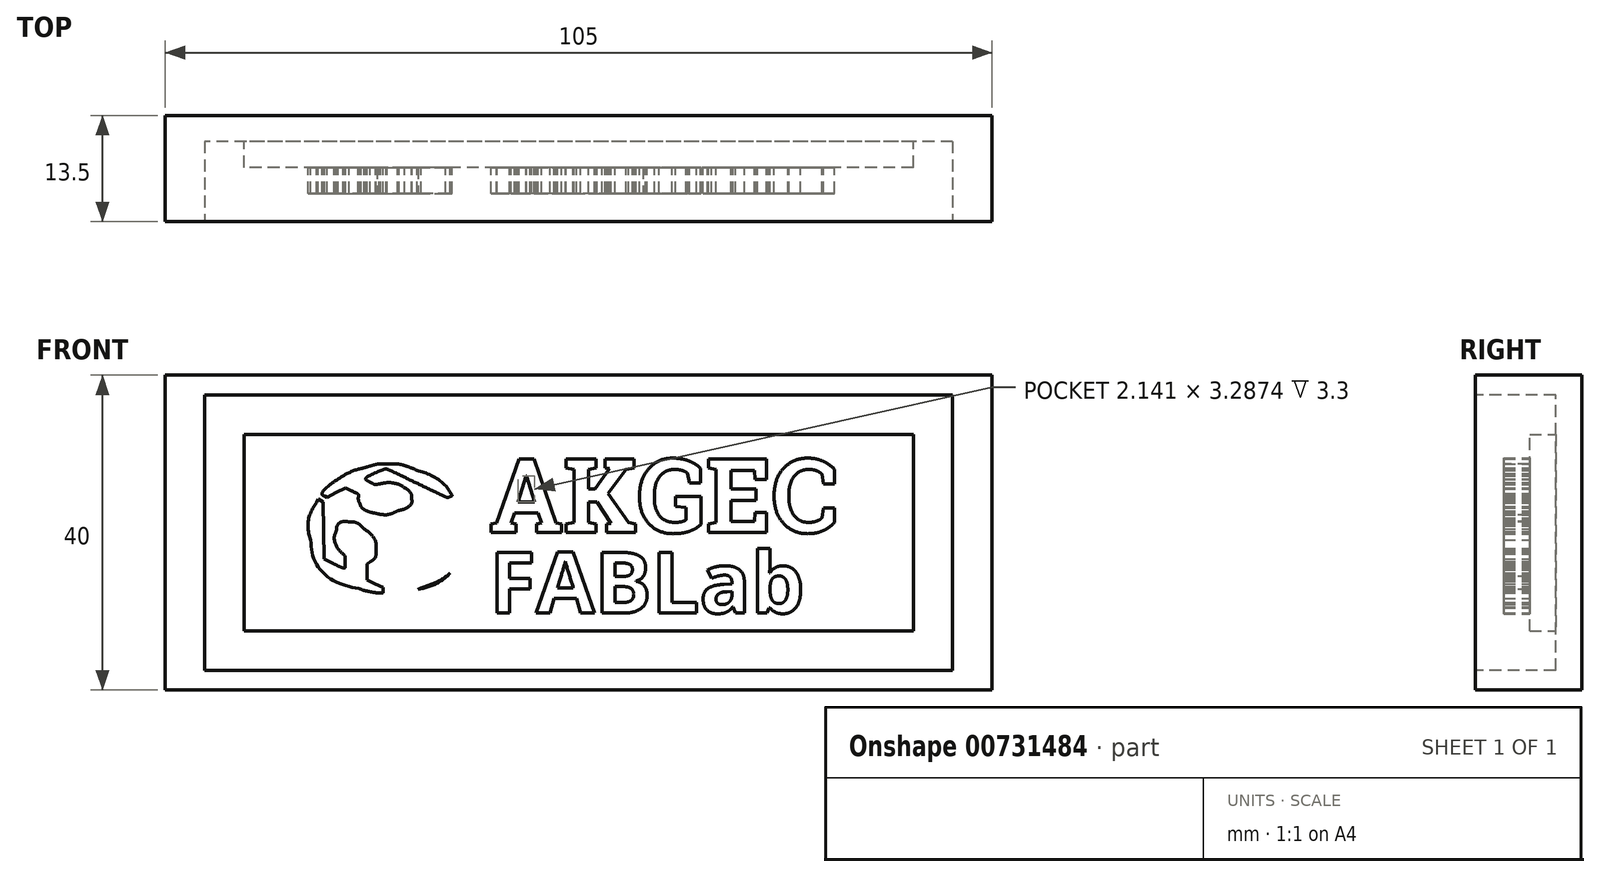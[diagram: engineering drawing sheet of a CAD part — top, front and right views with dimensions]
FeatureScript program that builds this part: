
annotation { "Feature Type Name" : "Feature", "Feature Type Description" : "" }
export const myFeature = defineFeature(function(context is Context, id is Id, definition is map)
    precondition{}
    {
        {
            var Q0;
            Q0=qCreatedBy(makeId("Front.planeOp"),FACE);
            var sketch = newSketch(context, id + "F0", { "sketchPlane" : qUnion([Q0])});
            skLineSegment(sketch, "E0.bottom", {"start": v(55, -20) * mm, "end": v(-50, -20) * mm});
            skLineSegment(sketch, "E0.top", {"start": v(55, 20) * mm, "end": v(-50, 20) * mm});
            skLineSegment(sketch, "E0.left", {"start": v(55, -20) * mm, "end": v(55, 20) * mm});
            skPoint(sketch, "E0.middle", {"position": v(0, 0) * mm});
            skLineSegment(sketch, "E1", {"start": v(-50, 20) * mm, "end": v(-50, -20) * mm});
            skPoint(sketch, "E2.orphan", {"position": v(-55, -20) * mm});
            skPoint(sketch, "E3.orphan", {"position": v(-55, 20) * mm});
            skSolve(sketch);
        }
        {
            var Q0;
            Q0 = qSketchRegion(id + "F0", true);
            extrude(context, id + "F1", {"entities" : qUnion([Q0]), "depth" : 13.5 * mm, "offsetDistance" : 25 * mm});
        }
        {
            var Q0;
            Q0=makeQuery(id+"F1.opExtrude","CAP_FACE",FACE,{"disambiguationData":[OSD([sQuery(id+"F0.wireOp",EDGE,"E0.bottom"),sQuery(id+"F0.wireOp",EDGE,"E0.top"),sQuery(id+"F0.wireOp",EDGE,"E0.left"),sQuery(id+"F0.wireOp",EDGE,"E0.right")])],"isStart":false});
            var sketch = newSketch(context, id + "F2", { "sketchPlane" : qUnion([Q0])});
            skLineSegment(sketch, "E4.bottom", {"start": v(50, -17.5) * mm, "end": v(-45, -17.5) * mm});
            skLineSegment(sketch, "E4.top", {"start": v(50, 17.5) * mm, "end": v(-45, 17.5) * mm});
            skLineSegment(sketch, "E4.left", {"start": v(50, -17.5) * mm, "end": v(50, 17.5) * mm});
            skPoint(sketch, "E4.middle", {"position": v(0, 0) * mm});
            skLineSegment(sketch, "E5", {"start": v(-45, 17.5) * mm, "end": v(-45, -17.5) * mm});
            skPoint(sketch, "E6.orphan", {"position": v(-50, -17.5) * mm});
            skPoint(sketch, "E7.orphan", {"position": v(-50, 17.5) * mm});
            skSolve(sketch);
        }
        {
            var Q0;
            Q0=makeQuery(id+"F2.imprint","IMPRINT",FACE,{"disambiguationData":[TD([[makeQuery(id+"F2.imprint","IMPRINT",EDGE,{"derivedFrom":sQuery(id+"F2.wireOp",EDGE,"E4.bottom")}),-1.0]])]});
            extrude(context, id + "F3", {"entities" : qUnion([Q0]), "operationType" : NewBodyOperationType.REMOVE, "oppositeDirection" : true, "depth" : 10.2 * mm, "offsetDistance" : 25 * mm});
        }
        {
            var Q0;
            Q0=makeQuery(id+"F3.boolean.opBoolean","COPY",FACE,{"derivedFrom":makeQuery(id+"F3.opExtrude","CAP_FACE",FACE,{"disambiguationData":[OSD([sQuery(id+"F2.wireOp",EDGE,"E4.bottom"),sQuery(id+"F2.wireOp",EDGE,"E4.top"),sQuery(id+"F2.wireOp",EDGE,"E4.left"),sQuery(id+"F2.wireOp",EDGE,"E4.right")])],"isStart":false})});
            var sketch = newSketch(context, id + "F4", { "sketchPlane" : qUnion([Q0])});
            skLineSegment(sketch, "E8.bottom", {"start": v(45, -12.5) * mm, "end": v(-40, -12.5) * mm});
            skLineSegment(sketch, "E8.top", {"start": v(45, 12.5) * mm, "end": v(-40, 12.5) * mm});
            skLineSegment(sketch, "E8.left", {"start": v(45, -12.5) * mm, "end": v(45, 12.5) * mm});
            skPoint(sketch, "E8.middle", {"position": v(0, 0) * mm});
            skLineSegment(sketch, "E9", {"start": v(-40, 12.5) * mm, "end": v(-40, -12.5) * mm});
            skPoint(sketch, "E8.right.end.orphan", {"position": v(-45, 12.5) * mm});
            skPoint(sketch, "E10.orphan", {"position": v(-45, -12.5) * mm});
            skSolve(sketch);
        }
        {
            var Q0;
            Q0=makeQuery(id+"F4.imprint","IMPRINT",FACE,{"disambiguationData":[TD([[makeQuery(id+"F4.imprint","IMPRINT",EDGE,{"derivedFrom":sQuery(id+"F4.wireOp",EDGE,"E8.bottom")}),-1.0]])]});
            extrude(context, id + "F5", {"entities" : qUnion([Q0]), "operationType" : NewBodyOperationType.ADD, "depth" : 3.3 * mm, "offsetDistance" : 25 * mm});
        }
        {
            var Q0;
            Q0=makeQuery(id+"F5.opExtrude","CAP_FACE",FACE,{"disambiguationData":[OSD([sQuery(id+"F4.wireOp",EDGE,"E8.bottom"),sQuery(id+"F4.wireOp",EDGE,"E8.top"),sQuery(id+"F4.wireOp",EDGE,"E8.left"),sQuery(id+"F4.wireOp",EDGE,"E8.right")])],"isStart":false});
            var sketch = newSketch(context, id + "F6", { "sketchPlane" : qUnion([Q0])});
            skText(sketch, "E11", { "text": "AKGEC\n", "fontName": "RobotoSlab-Bold.ttf"});
            const initialGuessF6  = {"E11": [-0.00887, 0, 1, 0, 0.00945]};
            skSetInitialGuess(sketch, initialGuessF6);
            skSolve(sketch);
        }
        {
            var Q0;
            Q0=makeQuery(id+"F6.imprint","IMPRINT",FACE,{"disambiguationData":[TD([[makeQuery(id+"F6.imprint","IMPRINT",EDGE,{"derivedFrom":sQuery(id+"F6.wireOp",EDGE,"E11.sketch_text.stroke-0")}),1.0]])]});
            var sketch = newSketch(context, id + "F7", { "sketchPlane" : qUnion([Q0])});
            skText(sketch, "E12", { "text": "FABLab", "fontName": "OpenSans-Bold.ttf"});
            const initialGuessF7  = {"E12": [-0.00883, -0.01021, 1, 0, 0.00776]};
            skSetInitialGuess(sketch, initialGuessF7);
            skSolve(sketch);
        }
        {
            var Q0;
            Q0 = qSketchRegion(id + "F6", true);
            extrude(context, id + "F8", {"entities" : qUnion([Q0]), "operationType" : NewBodyOperationType.ADD, "depth" : 3.3 * mm, "offsetDistance" : 25 * mm});
        }
        {
            var Q0;
            Q0 = qSketchRegion(id + "F7", true);
            extrude(context, id + "F9", {"entities" : qUnion([Q0]), "operationType" : NewBodyOperationType.ADD, "depth" : 3.3 * mm, "offsetDistance" : 25 * mm});
        }
        {
            var Q0;
            {var subQ53=sQuery(id+"F4.wireOp",EDGE,"E8.left");var subQ57=sQuery(id+"F4.wireOp",EDGE,"E8.top");var subQ61=sQuery(id+"F4.wireOp",EDGE,"E8.right");var subQ68=sQuery(id+"F4.wireOp",EDGE,"E8.bottom");var subQ69=makeQuery(id+"F5.opExtrude","SWEPT_FACE",FACE,{"disambiguationData":[OSD([subQ68])]});Q0=makeQuery(id+"F9.boolean.opBoolean","SPLIT",FACE,{"disambiguationData":[TD([subQ69])],"derivedFrom":makeQuery(id+"F8.boolean.opBoolean","SPLIT",FACE,{"disambiguationData":[TD([subQ69])],"derivedFrom":makeQuery(id+"F5.opExtrude","CAP_FACE",FACE,{"disambiguationData":[OSD([subQ68,subQ57,subQ53,subQ61])],"isStart":false})})});}
            var sketch = newSketch(context, id + "F10", { "sketchPlane" : qUnion([Q0])});
            skFitSpline(sketch, "E13", {"points": [v(-25.16, -9.86) * mm, v(-25.16, -8.7) * mm, v(-25.14, -8.5) * mm, v(-25, -8.45) * mm]});
            skFitSpline(sketch, "E14", {"points": [v(-25, -8.45) * mm, v(-24.7, -8.36) * mm, v(-23.55, -8.4) * mm, v(-23.2, -8.52) * mm]});
            skFitSpline(sketch, "E15", {"points": [v(-23.2, -8.52) * mm, v(-22.66, -8.7) * mm, v(-22.49, -9.17) * mm, v(-22.81, -9.55) * mm]});
            skFitSpline(sketch, "E16", {"points": [v(-22.81, -9.55) * mm, v(-22.92, -9.67) * mm, v(-22.94, -9.77) * mm, v(-22.88, -9.8) * mm]});
            skFitSpline(sketch, "E17", {"points": [v(-22.88, -9.8) * mm, v(-22.83, -9.83) * mm, v(-22.73, -9.94) * mm, v(-22.67, -10.04) * mm]});
            skFitSpline(sketch, "E18", {"points": [v(-22.67, -10.04) * mm, v(-22.33, -10.56) * mm, v(-22.77, -11.1) * mm, v(-23.64, -11.23) * mm]});
            skFitSpline(sketch, "E19", {"points": [v(-23.64, -11.23) * mm, v(-23.94, -11.28) * mm, v(-24.26, -11.3) * mm, v(-24.35, -11.3) * mm]});
            skFitSpline(sketch, "E20", {"points": [v(-24.35, -11.3) * mm, v(-24.44, -11.3) * mm, v(-24.66, -11.27) * mm, v(-24.84, -11.25) * mm]});
            skLineSegment(sketch, "E21", {"start": v(-24.84, -11.25) * mm, "end": v(-25.16, -11.22) * mm});
            skLineSegment(sketch, "E22", {"start": v(-25.16, -11.22) * mm, "end": v(-25.16, -9.86) * mm});
            skFitSpline(sketch, "E23", {"points": [v(-23.1, -10.81) * mm, v(-22.95, -10.7) * mm, v(-22.85, -10.52) * mm, v(-22.85, -10.39) * mm]});
            skFitSpline(sketch, "E24", {"points": [v(-22.85, -10.39) * mm, v(-22.85, -10.16) * mm, v(-23.07, -9.9) * mm, v(-23.26, -9.9) * mm]});
            skFitSpline(sketch, "E25", {"points": [v(-23.26, -9.9) * mm, v(-23.44, -9.9) * mm, v(-23.36, -9.6) * mm, v(-23.15, -9.5) * mm]});
            skFitSpline(sketch, "E26", {"points": [v(-23.15, -9.5) * mm, v(-22.89, -9.36) * mm, v(-22.9, -9.03) * mm, v(-23.17, -8.82) * mm]});
            skFitSpline(sketch, "E27", {"points": [v(-23.17, -8.82) * mm, v(-23.35, -8.68) * mm, v(-23.53, -8.65) * mm, v(-24.13, -8.65) * mm]});
            skFitSpline(sketch, "E28", {"points": [v(-24.1, -11.04) * mm, v(-23.5, -11.01) * mm, v(-23.3, -10.97) * mm, v(-23.1, -10.81) * mm]});
            skLineSegment(sketch, "E29", {"start": v(-24.13, -8.65) * mm, "end": v(-24.86, -8.65) * mm});
            skLineSegment(sketch, "E30", {"start": v(-24.86, -8.65) * mm, "end": v(-24.86, -9.87) * mm});
            skLineSegment(sketch, "E31", {"start": v(-24.86, -9.87) * mm, "end": v(-24.86, -11.08) * mm});
            skLineSegment(sketch, "E32", {"start": v(-24.86, -11.08) * mm, "end": v(-24.1, -11.04) * mm});
            skFitSpline(sketch, "E33", {"points": [v(-23.99, -9.91) * mm, v(-23.6, -9.93) * mm, v(-23.49, -9.98) * mm, v(-23.36, -10.16) * mm]});
            skFitSpline(sketch, "E34", {"points": [v(-23.36, -10.16) * mm, v(-23.23, -10.35) * mm, v(-23.23, -10.4) * mm, v(-23.39, -10.6) * mm]});
            skFitSpline(sketch, "E35", {"points": [v(-23.39, -10.6) * mm, v(-23.53, -10.78) * mm, v(-23.64, -10.81) * mm, v(-24.01, -10.81) * mm]});
            skLineSegment(sketch, "E36", {"start": v(-24.46, -10.35) * mm, "end": v(-24.46, -9.89) * mm});
            skLineSegment(sketch, "E37", {"start": v(-24.46, -9.89) * mm, "end": v(-23.99, -9.91) * mm});
            skFitSpline(sketch, "E38", {"points": [v(-23.62, -10.45) * mm, v(-23.53, -10.33) * mm, v(-23.54, -10.28) * mm, v(-23.7, -10.18) * mm]});
            skFitSpline(sketch, "E39", {"points": [v(-23.7, -10.18) * mm, v(-24.02, -9.98) * mm, v(-24.16, -10.04) * mm, v(-24.16, -10.36) * mm]});
            skFitSpline(sketch, "E40", {"points": [v(-24.16, -10.36) * mm, v(-24.16, -10.62) * mm, v(-24.13, -10.65) * mm, v(-23.94, -10.63) * mm]});
            skFitSpline(sketch, "E41", {"points": [v(-23.94, -10.63) * mm, v(-23.82, -10.62) * mm, v(-23.68, -10.54) * mm, v(-23.62, -10.45) * mm]});
            skLineSegment(sketch, "E42", {"start": v(-24.01, -10.81) * mm, "end": v(-24.46, -10.81) * mm});
            skLineSegment(sketch, "E43", {"start": v(-24.46, -10.81) * mm, "end": v(-24.46, -10.35) * mm});
            skFitSpline(sketch, "E44", {"points": [v(-24.07, -8.82) * mm, v(-23.64, -8.82) * mm, v(-23.35, -8.98) * mm, v(-23.35, -9.23) * mm]});
            skFitSpline(sketch, "E45", {"points": [v(-23.35, -9.23) * mm, v(-23.35, -9.48) * mm, v(-23.64, -9.65) * mm, v(-24.07, -9.65) * mm]});
            skLineSegment(sketch, "E46", {"start": v(-24.46, -9.23) * mm, "end": v(-24.46, -8.82) * mm});
            skLineSegment(sketch, "E47", {"start": v(-24.46, -8.82) * mm, "end": v(-24.07, -8.82) * mm});
            skFitSpline(sketch, "E48", {"points": [v(-23.82, -9.43) * mm, v(-23.55, -9.35) * mm, v(-23.62, -9.07) * mm, v(-23.9, -9.07) * mm]});
            skFitSpline(sketch, "E49", {"points": [v(-23.9, -9.07) * mm, v(-24.1, -9.07) * mm, v(-24.16, -9.1) * mm, v(-24.16, -9.27) * mm]});
            skFitSpline(sketch, "E50", {"points": [v(-24.16, -9.27) * mm, v(-24.16, -9.49) * mm, v(-24.1, -9.52) * mm, v(-23.82, -9.43) * mm]});
            skLineSegment(sketch, "E51", {"start": v(-24.07, -9.65) * mm, "end": v(-24.46, -9.65) * mm});
            skLineSegment(sketch, "E52", {"start": v(-24.46, -9.65) * mm, "end": v(-24.46, -9.23) * mm});
            skFitSpline(sketch, "E53", {"points": [v(-15.81, -9.86) * mm, v(-15.81, -8.7) * mm, v(-15.79, -8.5) * mm, v(-15.65, -8.45) * mm]});
            skFitSpline(sketch, "E54", {"points": [v(-15.65, -8.45) * mm, v(-15.36, -8.36) * mm, v(-14.2, -8.4) * mm, v(-13.86, -8.52) * mm]});
            skFitSpline(sketch, "E55", {"points": [v(-13.86, -8.52) * mm, v(-13.3, -8.7) * mm, v(-13.13, -9.17) * mm, v(-13.46, -9.55) * mm]});
            skFitSpline(sketch, "E56", {"points": [v(-13.46, -9.55) * mm, v(-13.56, -9.67) * mm, v(-13.59, -9.77) * mm, v(-13.53, -9.8) * mm]});
            skFitSpline(sketch, "E57", {"points": [v(-13.53, -9.8) * mm, v(-13.47, -9.83) * mm, v(-13.38, -9.94) * mm, v(-13.31, -10.04) * mm]});
            skFitSpline(sketch, "E58", {"points": [v(-13.31, -10.04) * mm, v(-12.98, -10.56) * mm, v(-13.42, -11.1) * mm, v(-14.3, -11.23) * mm]});
            skFitSpline(sketch, "E59", {"points": [v(-14.3, -11.23) * mm, v(-14.6, -11.28) * mm, v(-14.9, -11.3) * mm, v(-15, -11.3) * mm]});
            skFitSpline(sketch, "E60", {"points": [v(-15, -11.3) * mm, v(-15.09, -11.3) * mm, v(-15.3, -11.27) * mm, v(-15.49, -11.25) * mm]});
            skLineSegment(sketch, "E61", {"start": v(-15.49, -11.25) * mm, "end": v(-15.81, -11.22) * mm});
            skLineSegment(sketch, "E62", {"start": v(-15.81, -11.22) * mm, "end": v(-15.81, -9.86) * mm});
            skFitSpline(sketch, "E63", {"points": [v(-13.75, -10.81) * mm, v(-13.6, -10.7) * mm, v(-13.5, -10.52) * mm, v(-13.5, -10.39) * mm]});
            skFitSpline(sketch, "E64", {"points": [v(-13.5, -10.39) * mm, v(-13.5, -10.16) * mm, v(-13.72, -9.9) * mm, v(-13.9, -9.9) * mm]});
            skFitSpline(sketch, "E65", {"points": [v(-13.9, -9.9) * mm, v(-14.08, -9.9) * mm, v(-14, -9.6) * mm, v(-13.8, -9.5) * mm]});
            skFitSpline(sketch, "E66", {"points": [v(-13.8, -9.5) * mm, v(-13.54, -9.36) * mm, v(-13.55, -9.03) * mm, v(-13.82, -8.82) * mm]});
            skFitSpline(sketch, "E67", {"points": [v(-13.82, -8.82) * mm, v(-14, -8.68) * mm, v(-14.18, -8.65) * mm, v(-14.78, -8.65) * mm]});
            skFitSpline(sketch, "E68", {"points": [v(-14.75, -11.04) * mm, v(-14.14, -11.01) * mm, v(-13.95, -10.97) * mm, v(-13.75, -10.81) * mm]});
            skLineSegment(sketch, "E69", {"start": v(-14.78, -8.65) * mm, "end": v(-15.51, -8.65) * mm});
            skLineSegment(sketch, "E70", {"start": v(-15.51, -8.65) * mm, "end": v(-15.51, -9.87) * mm});
            skLineSegment(sketch, "E71", {"start": v(-15.51, -9.87) * mm, "end": v(-15.51, -11.08) * mm});
            skLineSegment(sketch, "E72", {"start": v(-15.51, -11.08) * mm, "end": v(-14.75, -11.04) * mm});
            skFitSpline(sketch, "E73", {"points": [v(-14.63, -9.91) * mm, v(-14.24, -9.93) * mm, v(-14.13, -9.98) * mm, v(-14.01, -10.16) * mm]});
            skFitSpline(sketch, "E74", {"points": [v(-14.01, -10.16) * mm, v(-13.88, -10.35) * mm, v(-13.88, -10.4) * mm, v(-14.04, -10.6) * mm]});
            skFitSpline(sketch, "E75", {"points": [v(-14.04, -10.6) * mm, v(-14.18, -10.78) * mm, v(-14.28, -10.81) * mm, v(-14.66, -10.81) * mm]});
            skLineSegment(sketch, "E76", {"start": v(-15.1, -10.35) * mm, "end": v(-15.1, -9.89) * mm});
            skLineSegment(sketch, "E77", {"start": v(-15.1, -9.89) * mm, "end": v(-14.63, -9.91) * mm});
            skFitSpline(sketch, "E78", {"points": [v(-14.26, -10.45) * mm, v(-14.18, -10.33) * mm, v(-14.2, -10.28) * mm, v(-14.35, -10.18) * mm]});
            skFitSpline(sketch, "E79", {"points": [v(-14.35, -10.18) * mm, v(-14.67, -9.98) * mm, v(-14.8, -10.04) * mm, v(-14.8, -10.36) * mm]});
            skFitSpline(sketch, "E80", {"points": [v(-14.8, -10.36) * mm, v(-14.8, -10.62) * mm, v(-14.78, -10.65) * mm, v(-14.6, -10.63) * mm]});
            skFitSpline(sketch, "E81", {"points": [v(-14.6, -10.63) * mm, v(-14.47, -10.62) * mm, v(-14.33, -10.54) * mm, v(-14.26, -10.45) * mm]});
            skLineSegment(sketch, "E82", {"start": v(-14.66, -10.81) * mm, "end": v(-15.1, -10.81) * mm});
            skLineSegment(sketch, "E83", {"start": v(-15.1, -10.81) * mm, "end": v(-15.1, -10.35) * mm});
            skFitSpline(sketch, "E84", {"points": [v(-14.71, -8.82) * mm, v(-14.29, -8.82) * mm, v(-14, -8.98) * mm, v(-14, -9.23) * mm]});
            skFitSpline(sketch, "E85", {"points": [v(-14, -9.23) * mm, v(-14, -9.48) * mm, v(-14.29, -9.65) * mm, v(-14.71, -9.65) * mm]});
            skLineSegment(sketch, "E86", {"start": v(-15.1, -9.23) * mm, "end": v(-15.1, -8.82) * mm});
            skLineSegment(sketch, "E87", {"start": v(-15.1, -8.82) * mm, "end": v(-14.71, -8.82) * mm});
            skFitSpline(sketch, "E88", {"points": [v(-14.46, -9.43) * mm, v(-14.2, -9.35) * mm, v(-14.27, -9.07) * mm, v(-14.56, -9.07) * mm]});
            skFitSpline(sketch, "E89", {"points": [v(-14.56, -9.07) * mm, v(-14.76, -9.07) * mm, v(-14.8, -9.1) * mm, v(-14.8, -9.27) * mm]});
            skFitSpline(sketch, "E90", {"points": [v(-14.8, -9.27) * mm, v(-14.8, -9.49) * mm, v(-14.74, -9.52) * mm, v(-14.46, -9.43) * mm]});
            skLineSegment(sketch, "E91", {"start": v(-14.71, -9.65) * mm, "end": v(-15.1, -9.65) * mm});
            skLineSegment(sketch, "E92", {"start": v(-15.1, -9.65) * mm, "end": v(-15.1, -9.23) * mm});
            skFitSpline(sketch, "E93", {"points": [v(-28.89, -9.07) * mm, v(-29.46, -9.07) * mm, v(-29.49, -9.07) * mm, v(-29.49, -9.27) * mm]});
            skFitSpline(sketch, "E94", {"points": [v(-29.49, -9.27) * mm, v(-29.49, -9.47) * mm, v(-29.46, -9.48) * mm, v(-28.94, -9.48) * mm]});
            skFitSpline(sketch, "E95", {"points": [v(-28.94, -9.48) * mm, v(-28.43, -9.48) * mm, v(-28.38, -9.5) * mm, v(-28.32, -9.69) * mm]});
            skFitSpline(sketch, "E96", {"points": [v(-28.32, -9.69) * mm, v(-28.21, -10.06) * mm, v(-28.33, -10.15) * mm, v(-28.93, -10.15) * mm]});
            skLineSegment(sketch, "E97", {"start": v(-30.4, -9.81) * mm, "end": v(-30.4, -8.4) * mm});
            skLineSegment(sketch, "E98", {"start": v(-30.4, -8.4) * mm, "end": v(-29.34, -8.4) * mm});
            skLineSegment(sketch, "E99", {"start": v(-29.34, -8.4) * mm, "end": v(-28.28, -8.4) * mm});
            skLineSegment(sketch, "E100", {"start": v(-28.28, -8.4) * mm, "end": v(-28.28, -8.73) * mm});
            skLineSegment(sketch, "E101", {"start": v(-28.28, -8.73) * mm, "end": v(-28.28, -9.07) * mm});
            skLineSegment(sketch, "E102", {"start": v(-28.28, -9.07) * mm, "end": v(-28.89, -9.07) * mm});
            skLineSegment(sketch, "E103", {"start": v(-28.93, -10.15) * mm, "end": v(-29.49, -10.15) * mm});
            skLineSegment(sketch, "E104", {"start": v(-29.49, -10.15) * mm, "end": v(-29.49, -10.69) * mm});
            skLineSegment(sketch, "E105", {"start": v(-29.49, -10.69) * mm, "end": v(-29.49, -11.23) * mm});
            skLineSegment(sketch, "E106", {"start": v(-29.49, -11.23) * mm, "end": v(-29.94, -11.23) * mm});
            skLineSegment(sketch, "E107", {"start": v(-29.94, -11.23) * mm, "end": v(-30.4, -11.23) * mm});
            skLineSegment(sketch, "E108", {"start": v(-30.4, -11.23) * mm, "end": v(-30.4, -9.81) * mm});
            skFitSpline(sketch, "E109", {"points": [v(-29.14, -9.98) * mm, v(-28.71, -9.98) * mm, v(-28.58, -9.95) * mm, v(-28.58, -9.86) * mm]});
            skFitSpline(sketch, "E110", {"points": [v(-28.58, -9.86) * mm, v(-28.58, -9.76) * mm, v(-28.71, -9.73) * mm, v(-29.14, -9.73) * mm]});
            skLineSegment(sketch, "E111", {"start": v(-29.69, -10.52) * mm, "end": v(-29.69, -9.98) * mm});
            skLineSegment(sketch, "E112", {"start": v(-29.69, -9.98) * mm, "end": v(-29.14, -9.98) * mm});
            skFitSpline(sketch, "E113", {"points": [v(-29.09, -8.9) * mm, v(-28.62, -8.9) * mm, v(-28.48, -8.87) * mm, v(-28.48, -8.77) * mm]});
            skFitSpline(sketch, "E114", {"points": [v(-28.48, -8.77) * mm, v(-28.48, -8.67) * mm, v(-28.64, -8.65) * mm, v(-29.34, -8.65) * mm]});
            skLineSegment(sketch, "E115", {"start": v(-29.14, -9.73) * mm, "end": v(-29.69, -9.73) * mm});
            skLineSegment(sketch, "E116", {"start": v(-29.69, -9.73) * mm, "end": v(-29.69, -9.31) * mm});
            skLineSegment(sketch, "E117", {"start": v(-29.69, -9.31) * mm, "end": v(-29.69, -8.9) * mm});
            skLineSegment(sketch, "E118", {"start": v(-29.69, -8.9) * mm, "end": v(-29.09, -8.9) * mm});
            skFitSpline(sketch, "E119", {"points": [v(-29.94, -11.06) * mm, v(-29.7, -11.06) * mm, v(-29.69, -11.04) * mm, v(-29.69, -10.52) * mm]});
            skLineSegment(sketch, "E120", {"start": v(-29.34, -8.65) * mm, "end": v(-30.2, -8.65) * mm});
            skLineSegment(sketch, "E121", {"start": v(-30.2, -8.65) * mm, "end": v(-30.2, -9.86) * mm});
            skLineSegment(sketch, "E122", {"start": v(-30.2, -9.86) * mm, "end": v(-30.2, -11.06) * mm});
            skLineSegment(sketch, "E123", {"start": v(-30.2, -11.06) * mm, "end": v(-29.94, -11.06) * mm});
            skFitSpline(sketch, "E124", {"points": [v(-28.48, -11.16) * mm, v(-28.48, -11.12) * mm, v(-28.42, -10.93) * mm, v(-28.34, -10.72) * mm]});
            skFitSpline(sketch, "E125", {"points": [v(-28.34, -10.72) * mm, v(-28.26, -10.52) * mm, v(-28.03, -9.91) * mm, v(-27.83, -9.37) * mm]});
            skFitSpline(sketch, "E126", {"points": [v(-25.86, -9.73) * mm, v(-25.59, -10.44) * mm, v(-25.37, -11.07) * mm, v(-25.37, -11.13) * mm]});
            skFitSpline(sketch, "E127", {"points": [v(-25.37, -11.13) * mm, v(-25.37, -11.2) * mm, v(-25.53, -11.23) * mm, v(-25.85, -11.23) * mm]});
            skFitSpline(sketch, "E128", {"points": [v(-25.85, -11.23) * mm, v(-26.33, -11.23) * mm, v(-26.34, -11.23) * mm, v(-26.46, -10.9) * mm]});
            skFitSpline(sketch, "E129", {"points": [v(-26.46, -10.9) * mm, v(-26.58, -10.57) * mm, v(-26.6, -10.55) * mm, v(-26.95, -10.58) * mm]});
            skFitSpline(sketch, "E130", {"points": [v(-26.95, -10.58) * mm, v(-27.29, -10.6) * mm, v(-27.33, -10.63) * mm, v(-27.4, -10.92) * mm]});
            skFitSpline(sketch, "E131", {"points": [v(-27.4, -10.92) * mm, v(-27.5, -11.23) * mm, v(-27.5, -11.23) * mm, v(-28, -11.23) * mm]});
            skFitSpline(sketch, "E132", {"points": [v(-28, -11.23) * mm, v(-28.26, -11.23) * mm, v(-28.48, -11.2) * mm, v(-28.48, -11.16) * mm]});
            skLineSegment(sketch, "E133", {"start": v(-27.83, -9.37) * mm, "end": v(-27.47, -8.4) * mm});
            skLineSegment(sketch, "E134", {"start": v(-27.47, -8.4) * mm, "end": v(-26.9, -8.42) * mm});
            skLineSegment(sketch, "E135", {"start": v(-26.9, -8.42) * mm, "end": v(-26.34, -8.44) * mm});
            skLineSegment(sketch, "E136", {"start": v(-26.34, -8.44) * mm, "end": v(-25.86, -9.73) * mm});
            skFitSpline(sketch, "E137", {"points": [v(-26.23, -10.75) * mm, v(-26.15, -11) * mm, v(-26.09, -11.06) * mm, v(-25.9, -11.06) * mm]});
            skFitSpline(sketch, "E138", {"points": [v(-25.9, -11.06) * mm, v(-25.77, -11.06) * mm, v(-25.67, -11.05) * mm, v(-25.67, -11.04) * mm]});
            skFitSpline(sketch, "E139", {"points": [v(-25.67, -11.04) * mm, v(-25.67, -11.03) * mm, v(-25.86, -10.5) * mm, v(-26.1, -9.86) * mm]});
            skLineSegment(sketch, "E140", {"start": v(-27.63, -10.73) * mm, "end": v(-27.56, -10.39) * mm});
            skLineSegment(sketch, "E141", {"start": v(-27.56, -10.39) * mm, "end": v(-26.94, -10.41) * mm});
            skLineSegment(sketch, "E142", {"start": v(-26.94, -10.41) * mm, "end": v(-26.32, -10.44) * mm});
            skLineSegment(sketch, "E143", {"start": v(-26.32, -10.44) * mm, "end": v(-26.23, -10.75) * mm});
            skFitSpline(sketch, "E144", {"points": [v(-27.6, -9.48) * mm, v(-27.75, -9.92) * mm, v(-27.95, -10.45) * mm, v(-28.03, -10.67) * mm]});
            skFitSpline(sketch, "E145", {"points": [v(-28.03, -10.67) * mm, v(-28.17, -11.06) * mm, v(-28.17, -11.06) * mm, v(-27.93, -11.06) * mm]});
            skFitSpline(sketch, "E146", {"points": [v(-27.93, -11.06) * mm, v(-27.73, -11.06) * mm, v(-27.68, -11) * mm, v(-27.63, -10.73) * mm]});
            skLineSegment(sketch, "E147", {"start": v(-26.1, -9.86) * mm, "end": v(-26.53, -8.7) * mm});
            skLineSegment(sketch, "E148", {"start": v(-26.53, -8.7) * mm, "end": v(-26.92, -8.7) * mm});
            skLineSegment(sketch, "E149", {"start": v(-26.92, -8.7) * mm, "end": v(-27.3, -8.7) * mm});
            skLineSegment(sketch, "E150", {"start": v(-27.3, -8.7) * mm, "end": v(-27.6, -9.48) * mm});
            skFitSpline(sketch, "E151", {"points": [v(-27.34, -9.83) * mm, v(-27.23, -9.27) * mm, v(-27.07, -8.9) * mm, v(-26.94, -8.9) * mm]});
            skFitSpline(sketch, "E152", {"points": [v(-26.94, -8.9) * mm, v(-26.86, -8.9) * mm, v(-26.73, -9.12) * mm, v(-26.64, -9.4) * mm]});
            skFitSpline(sketch, "E153", {"points": [v(-26.64, -9.4) * mm, v(-26.4, -10.13) * mm, v(-26.4, -10.15) * mm, v(-26.94, -10.15) * mm]});
            skLineSegment(sketch, "E154", {"start": v(-5.73, -9.43) * mm, "end": v(-5.73, -9.43) * mm});
            skFitSpline(sketch, "E155", {"points": [v(-26.81, -9.77) * mm, v(-26.85, -9.7) * mm, v(-26.88, -9.57) * mm, v(-26.88, -9.5) * mm]});
            skFitSpline(sketch, "E156", {"points": [v(-26.88, -9.5) * mm, v(-26.89, -9.38) * mm, v(-26.9, -9.39) * mm, v(-26.97, -9.52) * mm]});
            skFitSpline(sketch, "E157", {"points": [v(-26.97, -9.52) * mm, v(-27.1, -9.78) * mm, v(-27.09, -9.9) * mm, v(-26.91, -9.9) * mm]});
            skFitSpline(sketch, "E158", {"points": [v(-26.91, -9.9) * mm, v(-26.8, -9.9) * mm, v(-26.77, -9.85) * mm, v(-26.81, -9.77) * mm]});
            skLineSegment(sketch, "E159", {"start": v(-26.94, -10.15) * mm, "end": v(-27.4, -10.15) * mm});
            skLineSegment(sketch, "E160", {"start": v(-27.4, -10.15) * mm, "end": v(-27.34, -9.83) * mm});
            skLineSegment(sketch, "E161", {"start": v(-4.91, -8.47) * mm, "end": v(-4.91, -8.47) * mm});
            skFitSpline(sketch, "E162", {"points": [v(-20.9, -8.41) * mm, v(-20.66, -8.4) * mm, v(-20.48, -8.43) * mm, v(-20.43, -8.5) * mm]});
            skFitSpline(sketch, "E163", {"points": [v(-20.43, -8.5) * mm, v(-20.38, -8.56) * mm, v(-20.34, -9.05) * mm, v(-20.34, -9.59) * mm]});
            skLineSegment(sketch, "E164", {"start": v(-21.32, -9.83) * mm, "end": v(-21.3, -8.44) * mm});
            skLineSegment(sketch, "E165", {"start": v(-21.3, -8.44) * mm, "end": v(-20.9, -8.41) * mm});
            skFitSpline(sketch, "E166", {"points": [v(-19.73, -10.56) * mm, v(-19.15, -10.56) * mm, v(-19.13, -10.57) * mm, v(-19.12, -10.8) * mm]});
            skFitSpline(sketch, "E167", {"points": [v(-19.12, -10.8) * mm, v(-19.12, -11) * mm, v(-19.1, -10.99) * mm, v(-18.98, -10.69) * mm]});
            skFitSpline(sketch, "E168", {"points": [v(-18.98, -10.69) * mm, v(-18.9, -10.5) * mm, v(-18.68, -9.91) * mm, v(-18.48, -9.37) * mm]});
            skLineSegment(sketch, "E169", {"start": v(-20.34, -9.59) * mm, "end": v(-20.34, -10.56) * mm});
            skLineSegment(sketch, "E170", {"start": v(-20.34, -10.56) * mm, "end": v(-19.73, -10.56) * mm});
            skFitSpline(sketch, "E171", {"points": [v(-16.5, -9.73) * mm, v(-16.24, -10.44) * mm, v(-16.02, -11.07) * mm, v(-16.02, -11.13) * mm]});
            skFitSpline(sketch, "E172", {"points": [v(-16.02, -11.13) * mm, v(-16.01, -11.2) * mm, v(-16.18, -11.23) * mm, v(-16.5, -11.23) * mm]});
            skFitSpline(sketch, "E173", {"points": [v(-16.5, -11.23) * mm, v(-16.98, -11.23) * mm, v(-16.99, -11.23) * mm, v(-17.1, -10.9) * mm]});
            skFitSpline(sketch, "E174", {"points": [v(-17.1, -10.9) * mm, v(-17.23, -10.57) * mm, v(-17.25, -10.55) * mm, v(-17.6, -10.58) * mm]});
            skFitSpline(sketch, "E175", {"points": [v(-17.6, -10.58) * mm, v(-17.93, -10.6) * mm, v(-17.98, -10.63) * mm, v(-18.06, -10.92) * mm]});
            skLineSegment(sketch, "E176", {"start": v(-18.48, -9.37) * mm, "end": v(-18.11, -8.4) * mm});
            skLineSegment(sketch, "E177", {"start": v(-18.11, -8.4) * mm, "end": v(-17.55, -8.42) * mm});
            skLineSegment(sketch, "E178", {"start": v(-17.55, -8.42) * mm, "end": v(-16.99, -8.44) * mm});
            skLineSegment(sketch, "E179", {"start": v(-16.99, -8.44) * mm, "end": v(-16.5, -9.73) * mm});
            skFitSpline(sketch, "E180", {"points": [v(-19.33, -10.9) * mm, v(-19.33, -10.75) * mm, v(-19.4, -10.73) * mm, v(-19.99, -10.73) * mm]});
            skLineSegment(sketch, "E181", {"start": v(-18.06, -10.92) * mm, "end": v(-18.15, -11.23) * mm});
            skLineSegment(sketch, "E182", {"start": v(-18.15, -11.23) * mm, "end": v(-19.75, -11.23) * mm});
            skLineSegment(sketch, "E183", {"start": v(-19.75, -11.23) * mm, "end": v(-21.35, -11.23) * mm});
            skLineSegment(sketch, "E184", {"start": v(-21.35, -11.23) * mm, "end": v(-21.32, -9.83) * mm});
            skLineSegment(sketch, "E185", {"start": v(0.58, -8.53) * mm, "end": v(0.58, -8.53) * mm});
            skFitSpline(sketch, "E186", {"points": [v(-20.64, -9.69) * mm, v(-20.64, -8.7) * mm, v(-20.65, -8.65) * mm, v(-20.84, -8.65) * mm]});
            skFitSpline(sketch, "E187", {"points": [v(-20.84, -8.65) * mm, v(-21.03, -8.65) * mm, v(-21.04, -8.7) * mm, v(-21.04, -9.86) * mm]});
            skLineSegment(sketch, "E188", {"start": v(-19.99, -10.73) * mm, "end": v(-20.64, -10.73) * mm});
            skLineSegment(sketch, "E189", {"start": v(-20.64, -10.73) * mm, "end": v(-20.64, -9.69) * mm});
            skFitSpline(sketch, "E190", {"points": [v(-20.19, -11.06) * mm, v(-19.4, -11.06) * mm, v(-19.33, -11.05) * mm, v(-19.33, -10.9) * mm]});
            skLineSegment(sketch, "E191", {"start": v(-21.04, -9.86) * mm, "end": v(-21.04, -11.06) * mm});
            skLineSegment(sketch, "E192", {"start": v(-21.04, -11.06) * mm, "end": v(-20.19, -11.06) * mm});
            skFitSpline(sketch, "E193", {"points": [v(-16.88, -10.75) * mm, v(-16.8, -11) * mm, v(-16.74, -11.06) * mm, v(-16.55, -11.06) * mm]});
            skFitSpline(sketch, "E194", {"points": [v(-16.55, -11.06) * mm, v(-16.42, -11.06) * mm, v(-16.32, -11.05) * mm, v(-16.32, -11.04) * mm]});
            skFitSpline(sketch, "E195", {"points": [v(-16.32, -11.04) * mm, v(-16.32, -11.03) * mm, v(-16.51, -10.5) * mm, v(-16.75, -9.86) * mm]});
            skLineSegment(sketch, "E196", {"start": v(-18.28, -10.73) * mm, "end": v(-18.2, -10.39) * mm});
            skLineSegment(sketch, "E197", {"start": v(-18.2, -10.39) * mm, "end": v(-17.59, -10.41) * mm});
            skLineSegment(sketch, "E198", {"start": v(-17.59, -10.41) * mm, "end": v(-16.97, -10.44) * mm});
            skLineSegment(sketch, "E199", {"start": v(-16.97, -10.44) * mm, "end": v(-16.88, -10.75) * mm});
            skFitSpline(sketch, "E200", {"points": [v(-18.24, -9.48) * mm, v(-18.4, -9.92) * mm, v(-18.6, -10.45) * mm, v(-18.67, -10.67) * mm]});
            skFitSpline(sketch, "E201", {"points": [v(-18.67, -10.67) * mm, v(-18.82, -11.06) * mm, v(-18.82, -11.06) * mm, v(-18.58, -11.06) * mm]});
            skFitSpline(sketch, "E202", {"points": [v(-18.58, -11.06) * mm, v(-18.38, -11.06) * mm, v(-18.33, -11) * mm, v(-18.28, -10.73) * mm]});
            skLineSegment(sketch, "E203", {"start": v(-16.75, -9.86) * mm, "end": v(-17.18, -8.7) * mm});
            skLineSegment(sketch, "E204", {"start": v(-17.18, -8.7) * mm, "end": v(-17.57, -8.7) * mm});
            skLineSegment(sketch, "E205", {"start": v(-17.57, -8.7) * mm, "end": v(-17.95, -8.7) * mm});
            skLineSegment(sketch, "E206", {"start": v(-17.95, -8.7) * mm, "end": v(-18.24, -9.48) * mm});
            skFitSpline(sketch, "E207", {"points": [v(-17.99, -9.83) * mm, v(-17.88, -9.27) * mm, v(-17.72, -8.9) * mm, v(-17.58, -8.9) * mm]});
            skFitSpline(sketch, "E208", {"points": [v(-17.58, -8.9) * mm, v(-17.51, -8.9) * mm, v(-17.38, -9.12) * mm, v(-17.29, -9.4) * mm]});
            skFitSpline(sketch, "E209", {"points": [v(-17.29, -9.4) * mm, v(-17.04, -10.13) * mm, v(-17.05, -10.15) * mm, v(-17.59, -10.15) * mm]});
            skLineSegment(sketch, "E210", {"start": v(3.62, -9.43) * mm, "end": v(3.62, -9.43) * mm});
            skFitSpline(sketch, "E211", {"points": [v(-17.46, -9.77) * mm, v(-17.5, -9.7) * mm, v(-17.53, -9.57) * mm, v(-17.53, -9.5) * mm]});
            skFitSpline(sketch, "E212", {"points": [v(-17.53, -9.5) * mm, v(-17.54, -9.38) * mm, v(-17.55, -9.39) * mm, v(-17.62, -9.52) * mm]});
            skFitSpline(sketch, "E213", {"points": [v(-17.62, -9.52) * mm, v(-17.76, -9.78) * mm, v(-17.74, -9.9) * mm, v(-17.56, -9.9) * mm]});
            skFitSpline(sketch, "E214", {"points": [v(-17.56, -9.9) * mm, v(-17.46, -9.9) * mm, v(-17.42, -9.85) * mm, v(-17.46, -9.77) * mm]});
            skLineSegment(sketch, "E215", {"start": v(-17.59, -10.15) * mm, "end": v(-18.05, -10.15) * mm});
            skLineSegment(sketch, "E216", {"start": v(-18.05, -10.15) * mm, "end": v(-17.99, -9.83) * mm});
            skFitSpline(sketch, "E217", {"points": [v(-23.95, -7.69) * mm, v(-27.63, -7.03) * mm, v(-30.47, -4.85) * mm, v(-31.56, -1.85) * mm]});
            skFitSpline(sketch, "E218", {"points": [v(-31.56, -1.85) * mm, v(-31.94, -0.8) * mm, v(-32.01, 1.11) * mm, v(-31.72, 2.23) * mm]});
            skFitSpline(sketch, "E219", {"points": [v(-31.72, 2.23) * mm, v(-31.52, 2.97) * mm, v(-31.02, 4.07) * mm, v(-30.76, 4.38) * mm]});
            skFitSpline(sketch, "E220", {"points": [v(-30.76, 4.38) * mm, v(-30.63, 4.52) * mm, v(-30.6, 4.52) * mm, v(-30.16, 4.29) * mm]});
            skLineSegment(sketch, "E221", {"start": v(4.44, -8.47) * mm, "end": v(4.44, -8.47) * mm});
            skFitSpline(sketch, "E222", {"points": [v(-27.5, -3.6) * mm, v(-27.47, -3.05) * mm, v(-27.5, -2.96) * mm, v(-27.72, -2.71) * mm]});
            skFitSpline(sketch, "E223", {"points": [v(-27.72, -2.71) * mm, v(-28.25, -2.14) * mm, v(-28.51, -1.5) * mm, v(-28.56, -0.68) * mm]});
            skFitSpline(sketch, "E224", {"points": [v(-28.56, -0.68) * mm, v(-28.6, 0.03) * mm, v(-28.59, 0.13) * mm, v(-28.34, 0.54) * mm]});
            skFitSpline(sketch, "E225", {"points": [v(-28.34, 0.54) * mm, v(-27.97, 1.17) * mm, v(-27.54, 1.38) * mm, v(-26.67, 1.38) * mm]});
            skFitSpline(sketch, "E226", {"points": [v(-26.67, 1.38) * mm, v(-26.16, 1.37) * mm, v(-25.9, 1.32) * mm, v(-25.47, 1.14) * mm]});
            skFitSpline(sketch, "E227", {"points": [v(-25.47, 1.14) * mm, v(-23.88, 0.46) * mm, v(-22.74, -1.38) * mm, v(-23.05, -2.75) * mm]});
            skFitSpline(sketch, "E228", {"points": [v(-23.05, -2.75) * mm, v(-23.17, -3.26) * mm, v(-23.56, -3.79) * mm, v(-23.91, -3.92) * mm]});
            skFitSpline(sketch, "E229", {"points": [v(-23.91, -3.92) * mm, v(-24.15, -4.01) * mm, v(-24.16, -4.04) * mm, v(-24.16, -4.95) * mm]});
            skLineSegment(sketch, "E230", {"start": v(-30.16, 4.29) * mm, "end": v(-29.69, 4.04) * mm});
            skLineSegment(sketch, "E231", {"start": v(-29.69, 4.04) * mm, "end": v(-29.69, 0.42) * mm});
            skLineSegment(sketch, "E232", {"start": v(-29.69, 0.42) * mm, "end": v(-29.69, -3.2) * mm});
            skLineSegment(sketch, "E233", {"start": v(-29.69, -3.2) * mm, "end": v(-28.6, -3.72) * mm});
            skLineSegment(sketch, "E234", {"start": v(-28.6, -3.72) * mm, "end": v(-27.53, -4.23) * mm});
            skLineSegment(sketch, "E235", {"start": v(-27.53, -4.23) * mm, "end": v(-27.5, -3.6) * mm});
            skFitSpline(sketch, "E236", {"points": [v(-22.73, -7.8) * mm, v(-23.04, -7.8) * mm, v(-23.6, -7.75) * mm, v(-23.95, -7.69) * mm]});
            skLineSegment(sketch, "E237", {"start": v(-24.16, -4.95) * mm, "end": v(-24.16, -5.88) * mm});
            skLineSegment(sketch, "E238", {"start": v(-24.16, -5.88) * mm, "end": v(-23.15, -6.36) * mm});
            skLineSegment(sketch, "E239", {"start": v(-23.15, -6.36) * mm, "end": v(-22.15, -6.84) * mm});
            skLineSegment(sketch, "E240", {"start": v(-22.15, -6.84) * mm, "end": v(-22.15, -7.33) * mm});
            skLineSegment(sketch, "E241", {"start": v(-22.15, -7.33) * mm, "end": v(-22.15, -7.82) * mm});
            skLineSegment(sketch, "E242", {"start": v(-22.15, -7.82) * mm, "end": v(-22.73, -7.8) * mm});
            skLineSegment(sketch, "E243", {"start": v(-2.05, -6.39) * mm, "end": v(-2.05, -6.39) * mm});
            skFitSpline(sketch, "E244", {"points": [v(-24, -3.7) * mm, v(-23.5, -3.38) * mm, v(-23.26, -2.9) * mm, v(-23.26, -2.26) * mm]});
            skFitSpline(sketch, "E245", {"points": [v(-23.26, -2.26) * mm, v(-23.25, -1.29) * mm, v(-23.81, -0.28) * mm, v(-24.77, 0.46) * mm]});
            skFitSpline(sketch, "E246", {"points": [v(-24.77, 0.46) * mm, v(-26.18, 1.55) * mm, v(-27.88, 1.4) * mm, v(-28.3, 0.14) * mm]});
            skFitSpline(sketch, "E247", {"points": [v(-28.3, 0.14) * mm, v(-28.55, -0.64) * mm, v(-28.16, -1.91) * mm, v(-27.42, -2.71) * mm]});
            skFitSpline(sketch, "E248", {"points": [v(-27.42, -2.71) * mm, v(-27.2, -2.95) * mm, v(-27.18, -3.06) * mm, v(-27.18, -3.73) * mm]});
            skFitSpline(sketch, "E249", {"points": [v(-27.18, -3.73) * mm, v(-27.18, -4.4) * mm, v(-27.2, -4.49) * mm, v(-27.35, -4.48) * mm]});
            skFitSpline(sketch, "E250", {"points": [v(-27.35, -4.48) * mm, v(-27.45, -4.48) * mm, v(-28.05, -4.23) * mm, v(-28.68, -3.92) * mm]});
            skLineSegment(sketch, "E251", {"start": v(-22.35, -7.32) * mm, "end": v(-22.35, -6.99) * mm});
            skLineSegment(sketch, "E252", {"start": v(-22.35, -6.99) * mm, "end": v(-23.35, -6.5) * mm});
            skLineSegment(sketch, "E253", {"start": v(-23.35, -6.5) * mm, "end": v(-24.36, -6.03) * mm});
            skLineSegment(sketch, "E254", {"start": v(-24.36, -6.03) * mm, "end": v(-24.36, -4.99) * mm});
            skLineSegment(sketch, "E255", {"start": v(-24.36, -4.99) * mm, "end": v(-24.36, -3.95) * mm});
            skLineSegment(sketch, "E256", {"start": v(-24.36, -3.95) * mm, "end": v(-24, -3.7) * mm});
            skFitSpline(sketch, "E257", {"points": [v(-30.8, 3.86) * mm, v(-31.65, 2.27) * mm, v(-31.9, 0.69) * mm, v(-31.55, -0.94) * mm]});
            skFitSpline(sketch, "E258", {"points": [v(-31.55, -0.94) * mm, v(-30.96, -3.76) * mm, v(-28.62, -6.1) * mm, v(-25.41, -7.12) * mm]});
            skFitSpline(sketch, "E259", {"points": [v(-25.41, -7.12) * mm, v(-24.65, -7.35) * mm, v(-23.2, -7.63) * mm, v(-22.68, -7.64) * mm]});
            skFitSpline(sketch, "E260", {"points": [v(-22.68, -7.64) * mm, v(-22.36, -7.65) * mm, v(-22.35, -7.64) * mm, v(-22.35, -7.32) * mm]});
            skLineSegment(sketch, "E261", {"start": v(-28.68, -3.92) * mm, "end": v(-29.84, -3.36) * mm});
            skLineSegment(sketch, "E262", {"start": v(-29.84, -3.36) * mm, "end": v(-29.9, 0.28) * mm});
            skLineSegment(sketch, "E263", {"start": v(-29.9, 0.28) * mm, "end": v(-29.94, 3.93) * mm});
            skLineSegment(sketch, "E264", {"start": v(-29.94, 3.93) * mm, "end": v(-30.27, 4.1) * mm});
            skLineSegment(sketch, "E265", {"start": v(-30.27, 4.1) * mm, "end": v(-30.6, 4.27) * mm});
            skLineSegment(sketch, "E266", {"start": v(-30.6, 4.27) * mm, "end": v(-30.8, 3.86) * mm});
            skLineSegment(sketch, "E267", {"start": v(-0.45, -6.02) * mm, "end": v(-0.45, -6.02) * mm});
            skFitSpline(sketch, "E268", {"points": [v(-14.68, -1.2) * mm, v(-15.22, -1.46) * mm, v(-15.28, -1.52) * mm, v(-15.55, -2.08) * mm]});
            skFitSpline(sketch, "E269", {"points": [v(-15.55, -2.08) * mm, v(-16.09, -3.17) * mm, v(-17.32, -4.05) * mm, v(-18.44, -4.14) * mm]});
            skFitSpline(sketch, "E270", {"points": [v(-18.44, -4.14) * mm, v(-19.88, -4.25) * mm, v(-20.63, -3.62) * mm, v(-20.64, -2.31) * mm]});
            skFitSpline(sketch, "E271", {"points": [v(-20.64, -2.31) * mm, v(-20.64, -1.17) * mm, v(-20.02, -0.02) * mm, v(-19, 0.73) * mm]});
            skFitSpline(sketch, "E272", {"points": [v(-19, 0.73) * mm, v(-18.27, 1.25) * mm, v(-17.9, 1.38) * mm, v(-17.02, 1.38) * mm]});
            skFitSpline(sketch, "E273", {"points": [v(-17.02, 1.38) * mm, v(-16.4, 1.38) * mm, v(-16.21, 1.35) * mm, v(-15.94, 1.19) * mm]});
            skLineSegment(sketch, "E274", {"start": v(-21.73, -7.35) * mm, "end": v(-21.7, -6.86) * mm});
            skLineSegment(sketch, "E275", {"start": v(-21.7, -6.86) * mm, "end": v(-17.9, -5.03) * mm});
            skLineSegment(sketch, "E276", {"start": v(-17.9, -5.03) * mm, "end": v(-14.1, -3.2) * mm});
            skLineSegment(sketch, "E277", {"start": v(-14.1, -3.2) * mm, "end": v(-14.1, -2.05) * mm});
            skLineSegment(sketch, "E278", {"start": v(-14.1, -2.05) * mm, "end": v(-14.1, -0.91) * mm});
            skLineSegment(sketch, "E279", {"start": v(-14.1, -0.91) * mm, "end": v(-14.68, -1.2) * mm});
            skFitSpline(sketch, "E280", {"points": [v(-13.71, 4.24) * mm, v(-13.5, 4.34) * mm, v(-13.26, 4.42) * mm, v(-13.17, 4.42) * mm]});
            skFitSpline(sketch, "E281", {"points": [v(-13.17, 4.42) * mm, v(-12.9, 4.42) * mm, v(-12.2, 2.9) * mm, v(-11.99, 1.8) * mm]});
            skFitSpline(sketch, "E282", {"points": [v(-11.99, 1.8) * mm, v(-11.81, 0.9) * mm, v(-11.91, -0.85) * mm, v(-12.2, -1.7) * mm]});
            skFitSpline(sketch, "E283", {"points": [v(-12.2, -1.7) * mm, v(-12.95, -4) * mm, v(-14.85, -5.91) * mm, v(-17.5, -7.01) * mm]});
            skFitSpline(sketch, "E284", {"points": [v(-17.5, -7.01) * mm, v(-18.49, -7.43) * mm, v(-19.81, -7.73) * mm, v(-20.87, -7.8) * mm]});
            skLineSegment(sketch, "E285", {"start": v(-15.94, 1.19) * mm, "end": v(-15.61, 1) * mm});
            skLineSegment(sketch, "E286", {"start": v(-15.61, 1) * mm, "end": v(-14.88, 1.31) * mm});
            skLineSegment(sketch, "E287", {"start": v(-14.88, 1.31) * mm, "end": v(-14.15, 1.63) * mm});
            skLineSegment(sketch, "E288", {"start": v(-14.15, 1.63) * mm, "end": v(-14.13, 2.84) * mm});
            skLineSegment(sketch, "E289", {"start": v(-14.13, 2.84) * mm, "end": v(-14.1, 4.06) * mm});
            skLineSegment(sketch, "E290", {"start": v(-14.1, 4.06) * mm, "end": v(-13.71, 4.24) * mm});
            skFitSpline(sketch, "E291", {"points": [v(-19.48, -7.4) * mm, v(-15.96, -6.65) * mm, v(-13.36, -4.5) * mm, v(-12.37, -1.5) * mm]});
            skFitSpline(sketch, "E292", {"points": [v(-12.37, -1.5) * mm, v(-12.08, -0.62) * mm, v(-12.06, 1.44) * mm, v(-12.33, 2.3) * mm]});
            skFitSpline(sketch, "E293", {"points": [v(-12.33, 2.3) * mm, v(-12.57, 3.05) * mm, v(-13.1, 4.17) * mm, v(-13.22, 4.17) * mm]});
            skFitSpline(sketch, "E294", {"points": [v(-13.22, 4.17) * mm, v(-13.27, 4.17) * mm, v(-13.44, 4.11) * mm, v(-13.6, 4.04) * mm]});
            skLineSegment(sketch, "E295", {"start": v(-20.87, -7.8) * mm, "end": v(-21.76, -7.84) * mm});
            skLineSegment(sketch, "E296", {"start": v(-21.76, -7.84) * mm, "end": v(-21.73, -7.35) * mm});
            skLineSegment(sketch, "E297", {"start": v(0.17, -6.05) * mm, "end": v(0.17, -6.05) * mm});
            skFitSpline(sketch, "E298", {"points": [v(-16.1, 1.01) * mm, v(-16.52, 1.24) * mm, v(-16.63, 1.27) * mm, v(-17.13, 1.23) * mm]});
            skFitSpline(sketch, "E299", {"points": [v(-17.13, 1.23) * mm, v(-18.53, 1.13) * mm, v(-19.75, 0.1) * mm, v(-20.3, -1.45) * mm]});
            skFitSpline(sketch, "E300", {"points": [v(-20.3, -1.45) * mm, v(-20.5, -2.04) * mm, v(-20.45, -2.84) * mm, v(-20.17, -3.3) * mm]});
            skFitSpline(sketch, "E301", {"points": [v(-20.17, -3.3) * mm, v(-19.89, -3.75) * mm, v(-19.25, -4.01) * mm, v(-18.56, -3.96) * mm]});
            skFitSpline(sketch, "E302", {"points": [v(-18.56, -3.96) * mm, v(-17.3, -3.86) * mm, v(-16.13, -2.94) * mm, v(-15.62, -1.65) * mm]});
            skFitSpline(sketch, "E303", {"points": [v(-15.62, -1.65) * mm, v(-15.53, -1.42) * mm, v(-15.38, -1.3) * mm, v(-14.87, -1.05) * mm]});
            skFitSpline(sketch, "E304", {"points": [v(-14.87, -1.05) * mm, v(-13.86, -0.56) * mm, v(-13.9, -0.53) * mm, v(-13.92, -2.05) * mm]});
            skLineSegment(sketch, "E305", {"start": v(-13.6, 4.04) * mm, "end": v(-13.9, 3.91) * mm});
            skLineSegment(sketch, "E306", {"start": v(-13.9, 3.91) * mm, "end": v(-13.9, 2.72) * mm});
            skLineSegment(sketch, "E307", {"start": v(-13.9, 2.72) * mm, "end": v(-13.9, 1.52) * mm});
            skLineSegment(sketch, "E308", {"start": v(-13.9, 1.52) * mm, "end": v(-14.77, 1.14) * mm});
            skLineSegment(sketch, "E309", {"start": v(-14.77, 1.14) * mm, "end": v(-15.64, 0.75) * mm});
            skLineSegment(sketch, "E310", {"start": v(-15.64, 0.75) * mm, "end": v(-16.1, 1.01) * mm});
            skFitSpline(sketch, "E311", {"points": [v(-20.84, -7.62) * mm, v(-20.5, -7.58) * mm, v(-19.9, -7.49) * mm, v(-19.48, -7.4) * mm]});
            skLineSegment(sketch, "E312", {"start": v(-13.92, -2.05) * mm, "end": v(-13.95, -3.35) * mm});
            skLineSegment(sketch, "E313", {"start": v(-13.95, -3.35) * mm, "end": v(-17.67, -5.15) * mm});
            skLineSegment(sketch, "E314", {"start": v(-17.67, -5.15) * mm, "end": v(-21.4, -6.95) * mm});
            skLineSegment(sketch, "E315", {"start": v(-21.4, -6.95) * mm, "end": v(-21.43, -7.31) * mm});
            skLineSegment(sketch, "E316", {"start": v(-21.43, -7.31) * mm, "end": v(-21.46, -7.67) * mm});
            skLineSegment(sketch, "E317", {"start": v(-21.46, -7.67) * mm, "end": v(-20.84, -7.62) * mm});
            skFitSpline(sketch, "E318", {"points": [v(-23.28, 2.46) * mm, v(-24.06, 2.63) * mm, v(-24.74, 2.93) * mm, v(-25.18, 3.3) * mm]});
            skFitSpline(sketch, "E319", {"points": [v(-25.18, 3.3) * mm, v(-25.62, 3.68) * mm, v(-25.77, 3.97) * mm, v(-25.77, 4.44) * mm]});
            skFitSpline(sketch, "E320", {"points": [v(-25.77, 4.44) * mm, v(-25.77, 4.78) * mm, v(-25.79, 4.8) * mm, v(-26.42, 5.1) * mm]});
            skFitSpline(sketch, "E321", {"points": [v(-26.42, 5.1) * mm, v(-26.77, 5.28) * mm, v(-27.09, 5.42) * mm, v(-27.12, 5.42) * mm]});
            skFitSpline(sketch, "E322", {"points": [v(-27.12, 5.42) * mm, v(-27.15, 5.42) * mm, v(-27.65, 5.17) * mm, v(-28.23, 4.88) * mm]});
            skFitSpline(sketch, "E323", {"points": [v(-28.23, 4.88) * mm, v(-28.8, 4.58) * mm, v(-29.36, 4.34) * mm, v(-29.45, 4.34) * mm]});
            skFitSpline(sketch, "E324", {"points": [v(-29.45, 4.34) * mm, v(-29.72, 4.34) * mm, v(-30.4, 4.69) * mm, v(-30.4, 4.83) * mm]});
            skFitSpline(sketch, "E325", {"points": [v(-30.4, 4.83) * mm, v(-30.4, 5.03) * mm, v(-29.46, 6) * mm, v(-28.78, 6.53) * mm]});
            skFitSpline(sketch, "E326", {"points": [v(-28.78, 6.53) * mm, v(-27.6, 7.44) * mm, v(-26.04, 8.16) * mm, v(-24.49, 8.51) * mm]});
            skFitSpline(sketch, "E327", {"points": [v(-24.49, 8.51) * mm, v(-23.83, 8.67) * mm, v(-23.42, 8.7) * mm, v(-21.95, 8.7) * mm]});
            skFitSpline(sketch, "E328", {"points": [v(-21.95, 8.7) * mm, v(-20.41, 8.7) * mm, v(-20.08, 8.68) * mm, v(-19.33, 8.51) * mm]});
            skFitSpline(sketch, "E329", {"points": [v(-19.33, 8.51) * mm, v(-18.1, 8.24) * mm, v(-16.61, 7.61) * mm, v(-15.61, 6.94) * mm]});
            skFitSpline(sketch, "E330", {"points": [v(-15.61, 6.94) * mm, v(-14.68, 6.32) * mm, v(-13.4, 5.08) * mm, v(-13.4, 4.8) * mm]});
            skFitSpline(sketch, "E331", {"points": [v(-13.4, 4.8) * mm, v(-13.4, 4.67) * mm, v(-13.53, 4.57) * mm, v(-13.86, 4.43) * mm]});
            skFitSpline(sketch, "E332", {"points": [v(-18.03, 6.04) * mm, v(-20.08, 7.03) * mm, v(-21.8, 7.84) * mm, v(-21.84, 7.85) * mm]});
            skFitSpline(sketch, "E333", {"points": [v(-21.84, 7.85) * mm, v(-21.9, 7.86) * mm, v(-22.46, 7.63) * mm, v(-23.1, 7.33) * mm]});
            skLineSegment(sketch, "E334", {"start": v(-13.86, 4.43) * mm, "end": v(-14.32, 4.25) * mm});
            skLineSegment(sketch, "E335", {"start": v(-14.32, 4.25) * mm, "end": v(-18.03, 6.04) * mm});
            skFitSpline(sketch, "E336", {"points": [v(-23.84, 6.58) * mm, v(-23.46, 6.36) * mm, v(-23.4, 6.36) * mm, v(-22.31, 6.4) * mm]});
            skFitSpline(sketch, "E337", {"points": [v(-22.31, 6.4) * mm, v(-21.02, 6.44) * mm, v(-20.4, 6.33) * mm, v(-19.61, 5.92) * mm]});
            skFitSpline(sketch, "E338", {"points": [v(-19.61, 5.92) * mm, v(-18.65, 5.42) * mm, v(-18.25, 4.44) * mm, v(-18.71, 3.7) * mm]});
            skFitSpline(sketch, "E339", {"points": [v(-18.71, 3.7) * mm, v(-19, 3.24) * mm, v(-19.64, 2.8) * mm, v(-20.33, 2.58) * mm]});
            skFitSpline(sketch, "E340", {"points": [v(-20.33, 2.58) * mm, v(-21.06, 2.35) * mm, v(-22.47, 2.3) * mm, v(-23.28, 2.46) * mm]});
            skLineSegment(sketch, "E341", {"start": v(-23.1, 7.33) * mm, "end": v(-24.24, 6.8) * mm});
            skLineSegment(sketch, "E342", {"start": v(-24.24, 6.8) * mm, "end": v(-23.84, 6.58) * mm});
            skFitSpline(sketch, "E343", {"points": [v(-20.47, 2.77) * mm, v(-19.43, 3.09) * mm, v(-18.73, 3.75) * mm, v(-18.73, 4.4) * mm]});
            skFitSpline(sketch, "E344", {"points": [v(-18.73, 4.4) * mm, v(-18.73, 4.77) * mm, v(-19.2, 5.46) * mm, v(-19.61, 5.7) * mm]});
            skFitSpline(sketch, "E345", {"points": [v(-19.61, 5.7) * mm, v(-20.4, 6.15) * mm, v(-21.75, 6.35) * mm, v(-22.84, 6.18) * mm]});
            skFitSpline(sketch, "E346", {"points": [v(-22.84, 6.18) * mm, v(-23.37, 6.1) * mm, v(-23.4, 6.1) * mm, v(-23.98, 6.4) * mm]});
            skFitSpline(sketch, "E347", {"points": [v(-23.98, 6.4) * mm, v(-24.3, 6.57) * mm, v(-24.56, 6.75) * mm, v(-24.56, 6.8) * mm]});
            skFitSpline(sketch, "E348", {"points": [v(-24.56, 6.8) * mm, v(-24.56, 6.93) * mm, v(-22.03, 8.1) * mm, v(-21.83, 8.05) * mm]});
            skFitSpline(sketch, "E349", {"points": [v(-21.83, 8.05) * mm, v(-21.73, 8.03) * mm, v(-20.05, 7.24) * mm, v(-18.1, 6.3) * mm]});
            skFitSpline(sketch, "E350", {"points": [v(-18.1, 6.3) * mm, v(-16.15, 5.36) * mm, v(-14.48, 4.57) * mm, v(-14.39, 4.54) * mm]});
            skFitSpline(sketch, "E351", {"points": [v(-14.39, 4.54) * mm, v(-14.16, 4.47) * mm, v(-13.57, 4.73) * mm, v(-13.66, 4.86) * mm]});
            skFitSpline(sketch, "E352", {"points": [v(-13.66, 4.86) * mm, v(-14.5, 6.06) * mm, v(-16.29, 7.3) * mm, v(-18.03, 7.92) * mm]});
            skFitSpline(sketch, "E353", {"points": [v(-18.03, 7.92) * mm, v(-20.13, 8.66) * mm, v(-22.6, 8.78) * mm, v(-24.75, 8.23) * mm]});
            skFitSpline(sketch, "E354", {"points": [v(-24.75, 8.23) * mm, v(-25.8, 7.97) * mm, v(-27.16, 7.38) * mm, v(-28.03, 6.8) * mm]});
            skFitSpline(sketch, "E355", {"points": [v(-28.03, 6.8) * mm, v(-28.8, 6.3) * mm, v(-30.1, 5.1) * mm, v(-30.1, 4.89) * mm]});
            skFitSpline(sketch, "E356", {"points": [v(-30.1, 4.89) * mm, v(-30.1, 4.83) * mm, v(-29.95, 4.72) * mm, v(-29.78, 4.64) * mm]});
            skFitSpline(sketch, "E357", {"points": [v(-26.46, 5.36) * mm, v(-25.52, 4.9) * mm, v(-25.49, 4.88) * mm, v(-25.49, 4.43) * mm]});
            skFitSpline(sketch, "E358", {"points": [v(-25.49, 4.43) * mm, v(-25.49, 4.21) * mm, v(-25.42, 3.92) * mm, v(-25.33, 3.77) * mm]});
            skFitSpline(sketch, "E359", {"points": [v(-25.33, 3.77) * mm, v(-24.69, 2.75) * mm, v(-22.2, 2.23) * mm, v(-20.47, 2.77) * mm]});
            skLineSegment(sketch, "E360", {"start": v(-29.78, 4.64) * mm, "end": v(-29.47, 4.49) * mm});
            skLineSegment(sketch, "E361", {"start": v(-29.47, 4.49) * mm, "end": v(-28.29, 5.08) * mm});
            skLineSegment(sketch, "E362", {"start": v(-28.29, 5.08) * mm, "end": v(-27.1, 5.67) * mm});
            skLineSegment(sketch, "E363", {"start": v(-27.1, 5.67) * mm, "end": v(-26.46, 5.36) * mm});
            skSolve(sketch);
        }
        {
            var Q0;
            Q0=makeQuery(id+"F10.imprint","IMPRINT",FACE,{"disambiguationData":[TD([[makeQuery(id+"F10.imprint","IMPRINT",EDGE,{"derivedFrom":sQuery(id+"F10.wireOp",EDGE,"E343")}),1.0]])]});
            var Q1;
            Q1=makeQuery(id+"F10.imprint","IMPRINT",FACE,{"disambiguationData":[TD([[makeQuery(id+"F10.imprint","IMPRINT",EDGE,{"derivedFrom":sQuery(id+"F10.wireOp",EDGE,"E244")}),1.0]])]});
            var Q2;
            Q2=makeQuery(id+"F10.imprint","IMPRINT",FACE,{"disambiguationData":[TD([[makeQuery(id+"F10.imprint","IMPRINT",EDGE,{"derivedFrom":sQuery(id+"F10.wireOp",EDGE,"E291")}),1.0]])]});
            extrude(context, id + "F11", {"entities" : qUnion([Q0, Q1, Q2]), "operationType" : NewBodyOperationType.ADD, "depth" : 3.3 * mm, "offsetDistance" : 25 * mm});
        }
    });
